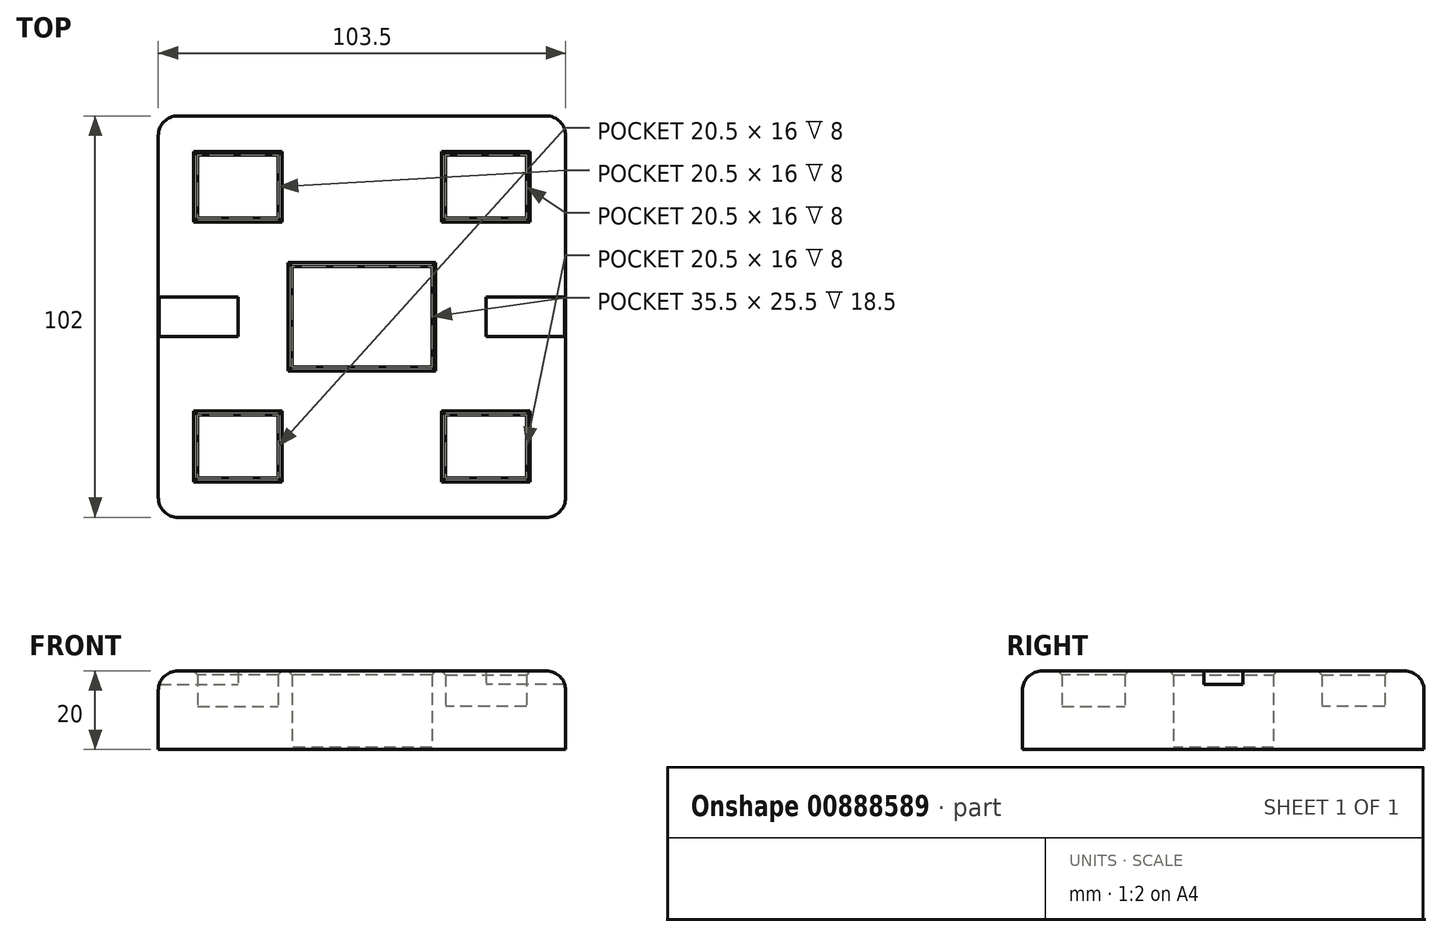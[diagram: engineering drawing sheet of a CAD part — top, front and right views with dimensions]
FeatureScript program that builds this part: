
annotation { "Feature Type Name" : "Feature", "Feature Type Description" : "" }
export const myFeature = defineFeature(function(context is Context, id is Id, definition is map)
    precondition{}
    {
        {
            var Q0;
            Q0=qCreatedBy(makeId("Top.planeOp"),FACE);
            var sketch = newSketch(context, id + "F0", { "sketchPlane" : qUnion([Q0])});
            skLineSegment(sketch, "E0.bottom", {"start": v(-46.75, 51) * mm, "end": v(46.75, 51) * mm});
            skLineSegment(sketch, "E0.top", {"start": v(-46.75, -51) * mm, "end": v(46.75, -51) * mm});
            skLineSegment(sketch, "E0.left", {"start": v(-51.75, 46) * mm, "end": v(-51.75, -46) * mm});
            skLineSegment(sketch, "E0.right", {"start": v(51.75, 46) * mm, "end": v(51.75, -46) * mm});
            skPoint(sketch, "E0.middle", {"position": v(0, 0) * mm});
            skLineSegment(sketch, "E1", {"start": v(-41.75, 51) * mm, "end": v(-41.75, -51) * mm});
            skLineSegment(sketch, "E2", {"start": v(-51.75, 41) * mm, "end": v(51.75, 41) * mm});
            skLineSegment(sketch, "E3", {"start": v(41.75, 51) * mm, "end": v(41.75, -51) * mm});
            skLineSegment(sketch, "E4", {"start": v(-51.75, -41) * mm, "end": v(51.75, -41) * mm});
            skLineSegment(sketch, "E5.bottom", {"start": v(-41.75, 41) * mm, "end": v(-21.25, 41) * mm});
            skLineSegment(sketch, "E5.top", {"start": v(-41.75, 25) * mm, "end": v(-21.25, 25) * mm});
            skLineSegment(sketch, "E5.left", {"start": v(-41.75, 41) * mm, "end": v(-41.75, 25) * mm});
            skLineSegment(sketch, "E5.right", {"start": v(-21.25, 41) * mm, "end": v(-21.25, 25) * mm});
            skLineSegment(sketch, "E6.bottom", {"start": v(41.75, 41) * mm, "end": v(21.25, 41) * mm});
            skLineSegment(sketch, "E6.top", {"start": v(41.75, 25) * mm, "end": v(21.25, 25) * mm});
            skLineSegment(sketch, "E6.left", {"start": v(41.75, 41) * mm, "end": v(41.75, 25) * mm});
            skLineSegment(sketch, "E6.right", {"start": v(21.25, 41) * mm, "end": v(21.25, 25) * mm});
            skLineSegment(sketch, "E7.bottom", {"start": v(-41.75, -41) * mm, "end": v(-21.25, -41) * mm});
            skLineSegment(sketch, "E7.top", {"start": v(-41.75, -25) * mm, "end": v(-21.25, -25) * mm});
            skLineSegment(sketch, "E7.left", {"start": v(-41.75, -41) * mm, "end": v(-41.75, -25) * mm});
            skLineSegment(sketch, "E7.right", {"start": v(-21.25, -41) * mm, "end": v(-21.25, -25) * mm});
            skLineSegment(sketch, "E8.bottom", {"start": v(41.75, -41) * mm, "end": v(21.25, -41) * mm});
            skLineSegment(sketch, "E8.top", {"start": v(41.75, -25) * mm, "end": v(21.25, -25) * mm});
            skLineSegment(sketch, "E8.left", {"start": v(41.75, -41) * mm, "end": v(41.75, -25) * mm});
            skLineSegment(sketch, "E8.right", {"start": v(21.25, -41) * mm, "end": v(21.25, -25) * mm});
            skLineSegment(sketch, "E9.bottom", {"start": v(17.75, 12.75) * mm, "end": v(-17.75, 12.75) * mm});
            skLineSegment(sketch, "E9.top", {"start": v(17.75, -12.75) * mm, "end": v(-17.75, -12.75) * mm});
            skLineSegment(sketch, "E9.left", {"start": v(17.75, 12.75) * mm, "end": v(17.75, -12.75) * mm});
            skLineSegment(sketch, "E9.right", {"start": v(-17.75, 12.75) * mm, "end": v(-17.75, -12.75) * mm});
            skPoint(sketch, "E10.visualSharp", {"position": v(-51.75, 51) * mm});
            skArc(sketch, "E10.filletArc", {"start": v(-46.75, 51) * mm, "mid": v(-50.29, 49.54) * mm, "end": v(-51.75, 46) * mm});
            skPoint(sketch, "E11.visualSharp", {"position": v(51.75, 51) * mm});
            skArc(sketch, "E11.filletArc", {"start": v(51.75, 46) * mm, "mid": v(50.29, 49.54) * mm, "end": v(46.75, 51) * mm});
            skPoint(sketch, "E12.visualSharp", {"position": v(51.75, -51) * mm});
            skArc(sketch, "E12.filletArc", {"start": v(46.75, -51) * mm, "mid": v(50.29, -49.54) * mm, "end": v(51.75, -46) * mm});
            skPoint(sketch, "E13.visualSharp", {"position": v(-51.75, -51) * mm});
            skArc(sketch, "E13.filletArc", {"start": v(-51.75, -46) * mm, "mid": v(-50.29, -49.54) * mm, "end": v(-46.75, -51) * mm});
            skLineSegment(sketch, "E14.bottom", {"start": v(-51.75, -5) * mm, "end": v(-31.5, -5) * mm});
            skLineSegment(sketch, "E14.top", {"start": v(-51.75, 5) * mm, "end": v(-31.5, 5) * mm});
            skLineSegment(sketch, "E14.left", {"start": v(-51.75, -5) * mm, "end": v(-51.75, 5) * mm});
            skLineSegment(sketch, "E14.right", {"start": v(-31.5, -5) * mm, "end": v(-31.5, 5) * mm});
            skLineSegment(sketch, "E15.bottom", {"start": v(51.75, -5) * mm, "end": v(31.5, -5) * mm});
            skLineSegment(sketch, "E15.top", {"start": v(51.75, 5) * mm, "end": v(31.5, 5) * mm});
            skLineSegment(sketch, "E15.left", {"start": v(51.75, -5) * mm, "end": v(51.75, 5) * mm});
            skLineSegment(sketch, "E15.right", {"start": v(31.5, -5) * mm, "end": v(31.5, 5) * mm});
            skSolve(sketch);
        }
        {
            assignVariable(context, id + "F1", {"name" : "DickeP", "anyValue" : 20 * mm});
        }
        {
            var Q0;
            {var subQ0=sQuery(id+"F0.wireOp",EDGE,"E10.filletArc");Q0=makeQuery(id+"F0.imprint","IMPRINT",FACE,{"disambiguationData":[TD([[makeQuery(id+"F0.imprint","IMPRINT",EDGE,{"derivedFrom":subQ0}),1.0]])]});}
            var Q1;
            {var subQ4=sQuery(id+"F0.wireOp",EDGE,"E0.left");var subQ6=sQuery(id+"F0.wireOp",EDGE,"E14.top");var subQ8=makeQuery(id+"F0.imprint","INTERSECT",VERTEX,{"derivedFrom":[subQ4,subQ6]});Q1=makeQuery(id+"F0.imprint","IMPRINT",FACE,{"disambiguationData":[TD([[makeQuery(id+"F0.imprint","IMPRINT",EDGE,{"disambiguationData":[TD([[subQ8,1.0]])],"derivedFrom":subQ4}),1.0]])]});}
            var Q2;
            {var subQ1=sQuery(id+"F0.wireOp",EDGE,"E0.left");var subQ5=sQuery(id+"F0.wireOp",EDGE,"E14.bottom");var subQ8=makeQuery(id+"F0.imprint","INTERSECT",VERTEX,{"derivedFrom":[subQ1,subQ5]});Q2=makeQuery(id+"F0.imprint","IMPRINT",FACE,{"disambiguationData":[TD([[makeQuery(id+"F0.imprint","IMPRINT",EDGE,{"disambiguationData":[TD([[subQ8,-1.0]])],"derivedFrom":subQ1}),1.0]])]});}
            var Q3;
            {var subQ7=sQuery(id+"F0.wireOp",EDGE,"E13.filletArc");Q3=makeQuery(id+"F0.imprint","IMPRINT",FACE,{"disambiguationData":[TD([[makeQuery(id+"F0.imprint","IMPRINT",EDGE,{"derivedFrom":subQ7}),1.0]])]});}
            var Q4;
            {var subQ4=sQuery(id+"F0.wireOp",EDGE,"E0.top");var subQ7=sQuery(id+"F0.wireOp",EDGE,"E1");var subQ8=makeQuery(id+"F0.imprint","INTERSECT",VERTEX,{"derivedFrom":[subQ4,subQ7]});Q4=makeQuery(id+"F0.imprint","IMPRINT",FACE,{"disambiguationData":[TD([[makeQuery(id+"F0.imprint","IMPRINT",EDGE,{"disambiguationData":[TD([[subQ8,-1.0]])],"derivedFrom":subQ4}),1.0]])]});}
            var Q5;
            {var subQ0=sQuery(id+"F0.wireOp",EDGE,"E12.filletArc");Q5=makeQuery(id+"F0.imprint","IMPRINT",FACE,{"disambiguationData":[TD([[makeQuery(id+"F0.imprint","IMPRINT",EDGE,{"derivedFrom":subQ0}),1.0]])]});}
            var Q6;
            {var subQ2=sQuery(id+"F0.wireOp",EDGE,"E4");var subQ4=sQuery(id+"F0.wireOp",EDGE,"E0.right");var subQ5=makeQuery(id+"F0.imprint","INTERSECT",VERTEX,{"derivedFrom":[subQ4,subQ2]});Q6=makeQuery(id+"F0.imprint","IMPRINT",FACE,{"disambiguationData":[TD([[makeQuery(id+"F0.imprint","IMPRINT",EDGE,{"disambiguationData":[TD([[subQ5,1.0]])],"derivedFrom":subQ4}),-1.0]])]});}
            var Q7;
            {var subQ18=sQuery(id+"F0.wireOp",EDGE,"E5.top");Q7=makeQuery(id+"F0.imprint","IMPRINT",FACE,{"disambiguationData":[TD([[makeQuery(id+"F0.imprint","IMPRINT",EDGE,{"derivedFrom":subQ18}),-1.0]])]});}
            var Q8;
            {var subQ4=sQuery(id+"F0.wireOp",EDGE,"E2");var subQ6=sQuery(id+"F0.wireOp",EDGE,"E0.right");var subQ8=makeQuery(id+"F0.imprint","INTERSECT",VERTEX,{"derivedFrom":[subQ6,subQ4]});Q8=makeQuery(id+"F0.imprint","IMPRINT",FACE,{"disambiguationData":[TD([[makeQuery(id+"F0.imprint","IMPRINT",EDGE,{"disambiguationData":[TD([[subQ8,-1.0]])],"derivedFrom":subQ6}),-1.0]])]});}
            var Q9;
            {var subQ5=sQuery(id+"F0.wireOp",EDGE,"E1");var subQ6=sQuery(id+"F0.wireOp",EDGE,"E0.bottom");var subQ7=makeQuery(id+"F0.imprint","INTERSECT",VERTEX,{"derivedFrom":[subQ6,subQ5]});Q9=makeQuery(id+"F0.imprint","IMPRINT",FACE,{"disambiguationData":[TD([[makeQuery(id+"F0.imprint","IMPRINT",EDGE,{"disambiguationData":[TD([[subQ7,-1.0]])],"derivedFrom":subQ6}),-1.0]])]});}
            var Q10;
            {var subQ7=sQuery(id+"F0.wireOp",EDGE,"E11.filletArc");Q10=makeQuery(id+"F0.imprint","IMPRINT",FACE,{"disambiguationData":[TD([[makeQuery(id+"F0.imprint","IMPRINT",EDGE,{"derivedFrom":subQ7}),1.0]])]});}
            extrude(context, id + "F2", {"entities" : qUnion([Q0, Q1, Q2, Q3, Q4, Q5, Q6, Q7, Q8, Q9, Q10]), "depth" : getVariable(context, 'DickeP'), "offsetDistance" : 25 * mm});
        }
        {
            assignVariable(context, id + "F3", {"name" : "unterLochST", "anyValue" : 11 * mm});
        }
        {
            var Q0;
            {var subQ3=sQuery(id+"F0.wireOp",EDGE,"E5.top");Q0=makeQuery(id+"F0.imprint","IMPRINT",FACE,{"disambiguationData":[TD([[makeQuery(id+"F0.imprint","IMPRINT",EDGE,{"derivedFrom":subQ3}),1.0]])]});}
            var Q1;
            {var subQ4=sQuery(id+"F0.wireOp",EDGE,"E6.top");Q1=makeQuery(id+"F0.imprint","IMPRINT",FACE,{"disambiguationData":[TD([[makeQuery(id+"F0.imprint","IMPRINT",EDGE,{"derivedFrom":subQ4}),-1.0]])]});}
            var Q2;
            {var subQ0=sQuery(id+"F0.wireOp",EDGE,"E8.top");Q2=makeQuery(id+"F0.imprint","IMPRINT",FACE,{"disambiguationData":[TD([[makeQuery(id+"F0.imprint","IMPRINT",EDGE,{"derivedFrom":subQ0}),1.0]])]});}
            var Q3;
            {var subQ0=sQuery(id+"F0.wireOp",EDGE,"E7.top");Q3=makeQuery(id+"F0.imprint","IMPRINT",FACE,{"disambiguationData":[TD([[makeQuery(id+"F0.imprint","IMPRINT",EDGE,{"derivedFrom":subQ0}),-1.0]])]});}
            extrude(context, id + "F4", {"entities" : qUnion([Q0, Q1, Q2, Q3]), "operationType" : NewBodyOperationType.ADD, "depth" : getVariable(context, 'unterLochST'), "offsetDistance" : 25 * mm});
        }
        {
            assignVariable(context, id + "F5", {"name" : "unterLochRM", "anyValue" : 0.5});
        }
        {
            var Q0;
            Q0=makeQuery(id+"F0.imprint","IMPRINT",FACE,{"disambiguationData":[TD([[makeQuery(id+"F0.imprint","IMPRINT",EDGE,{"derivedFrom":sQuery(id+"F0.wireOp",EDGE,"E9.bottom")}),1.0]])]});
            extrude(context, id + "F6", {"entities" : qUnion([Q0]), "operationType" : NewBodyOperationType.ADD, "depth" : (getVariable(context, 'unterLochRM')) * mm, "offsetDistance" : 25 * mm});
        }
        {
            var Q0;
            {var subQ5=sQuery(id+"F0.wireOp",EDGE,"E14.right");Q0=makeQuery(id+"F0.imprint","IMPRINT",FACE,{"disambiguationData":[TD([[makeQuery(id+"F0.imprint","IMPRINT",EDGE,{"derivedFrom":subQ5}),1.0]])]});}
            var Q1;
            {var subQ0=sQuery(id+"F0.wireOp",EDGE,"E14.bottom");var subQ1=sQuery(id+"F0.wireOp",EDGE,"E0.left");var subQ2=makeQuery(id+"F0.imprint","INTERSECT",VERTEX,{"derivedFrom":[subQ1,subQ0]});Q1=makeQuery(id+"F0.imprint","IMPRINT",FACE,{"disambiguationData":[TD([[makeQuery(id+"F0.imprint","IMPRINT",EDGE,{"disambiguationData":[TD([[subQ2,1.0]])],"derivedFrom":subQ1}),1.0]])]});}
            var Q2;
            {var subQ5=sQuery(id+"F0.wireOp",EDGE,"E15.right");Q2=makeQuery(id+"F0.imprint","IMPRINT",FACE,{"disambiguationData":[TD([[makeQuery(id+"F0.imprint","IMPRINT",EDGE,{"derivedFrom":subQ5}),-1.0]])]});}
            var Q3;
            {var subQ0=sQuery(id+"F0.wireOp",EDGE,"E15.top");var subQ1=sQuery(id+"F0.wireOp",EDGE,"E0.right");var subQ2=makeQuery(id+"F0.imprint","INTERSECT",VERTEX,{"derivedFrom":[subQ1,subQ0]});Q3=makeQuery(id+"F0.imprint","IMPRINT",FACE,{"disambiguationData":[TD([[makeQuery(id+"F0.imprint","IMPRINT",EDGE,{"disambiguationData":[TD([[subQ2,-1.0]])],"derivedFrom":subQ1}),-1.0]])]});}
            extrude(context, id + "F7", {"entities" : qUnion([Q0, Q1, Q2, Q3]), "operationType" : NewBodyOperationType.ADD, "depth" : 16.5 * mm, "offsetDistance" : 25 * mm});
        }
        {
            var Q0;
            {var subQ0=sQuery(id+"F0.wireOp",EDGE,"E2");Q0=makeQuery(id+"F2.opExtrude","CAP_EDGE",EDGE,{"disambiguationData":[OSD([subQ0]),TDD([makeQuery(id+"F0.imprint","IMPRINT",EDGE,{"disambiguationData":[TD([[makeQuery(id+"F0.imprint","INTERSECT",VERTEX,{"derivedFrom":[sQuery(id+"F0.wireOp",EDGE,"E1"),subQ0]}),-1.0]])],"derivedFrom":subQ0})])],"isStart":false});}
            var Q1;
            Q1=makeQuery(id+"F2.opExtrude","CAP_EDGE",EDGE,{"disambiguationData":[OSD([sQuery(id+"F0.wireOp",EDGE,"E5.right")])],"isStart":false});
            var Q2;
            {var subQ0=sQuery(id+"F0.wireOp",EDGE,"E1");Q2=makeQuery(id+"F2.opExtrude","CAP_EDGE",EDGE,{"disambiguationData":[OSD([subQ0]),TDD([makeQuery(id+"F0.imprint","IMPRINT",EDGE,{"disambiguationData":[TD([[makeQuery(id+"F0.imprint","INTERSECT",VERTEX,{"derivedFrom":[subQ0,sQuery(id+"F0.wireOp",EDGE,"E2")]}),-1.0]])],"derivedFrom":subQ0})])],"isStart":false});}
            var Q3;
            Q3=makeQuery(id+"F2.opExtrude","CAP_EDGE",EDGE,{"disambiguationData":[OSD([sQuery(id+"F0.wireOp",EDGE,"E5.top")])],"isStart":false});
            var Q4;
            {var subQ0=sQuery(id+"F0.wireOp",EDGE,"E2");Q4=makeQuery(id+"F2.opExtrude","CAP_EDGE",EDGE,{"disambiguationData":[OSD([subQ0]),TDD([makeQuery(id+"F0.imprint","IMPRINT",EDGE,{"disambiguationData":[TD([[makeQuery(id+"F0.imprint","INTERSECT",VERTEX,{"derivedFrom":[subQ0,sQuery(id+"F0.wireOp",EDGE,"E6.right")]}),-1.0]])],"derivedFrom":subQ0})])],"isStart":false});}
            var Q5;
            Q5=makeQuery(id+"F2.opExtrude","CAP_EDGE",EDGE,{"disambiguationData":[OSD([sQuery(id+"F0.wireOp",EDGE,"E6.right")])],"isStart":false});
            var Q6;
            Q6=makeQuery(id+"F2.opExtrude","CAP_EDGE",EDGE,{"disambiguationData":[OSD([sQuery(id+"F0.wireOp",EDGE,"E6.top")])],"isStart":false});
            var Q7;
            {var subQ0=sQuery(id+"F0.wireOp",EDGE,"E3");Q7=makeQuery(id+"F2.opExtrude","CAP_EDGE",EDGE,{"disambiguationData":[OSD([subQ0]),TDD([makeQuery(id+"F0.imprint","IMPRINT",EDGE,{"disambiguationData":[TD([[makeQuery(id+"F0.imprint","INTERSECT",VERTEX,{"derivedFrom":[subQ0,sQuery(id+"F0.wireOp",EDGE,"E6.top")]}),1.0]])],"derivedFrom":subQ0})])],"isStart":false});}
            var Q8;
            Q8=makeQuery(id+"F2.opExtrude","CAP_EDGE",EDGE,{"disambiguationData":[OSD([sQuery(id+"F0.wireOp",EDGE,"E8.top")])],"isStart":false});
            var Q9;
            Q9=makeQuery(id+"F2.opExtrude","CAP_EDGE",EDGE,{"disambiguationData":[OSD([sQuery(id+"F0.wireOp",EDGE,"E8.right")])],"isStart":false});
            var Q10;
            {var subQ0=sQuery(id+"F0.wireOp",EDGE,"E4");Q10=makeQuery(id+"F2.opExtrude","CAP_EDGE",EDGE,{"disambiguationData":[OSD([subQ0]),TDD([makeQuery(id+"F0.imprint","IMPRINT",EDGE,{"disambiguationData":[TD([[makeQuery(id+"F0.imprint","INTERSECT",VERTEX,{"derivedFrom":[subQ0,sQuery(id+"F0.wireOp",EDGE,"E8.right")]}),-1.0]])],"derivedFrom":subQ0})])],"isStart":false});}
            var Q11;
            {var subQ0=sQuery(id+"F0.wireOp",EDGE,"E3");Q11=makeQuery(id+"F2.opExtrude","CAP_EDGE",EDGE,{"disambiguationData":[OSD([subQ0]),TDD([makeQuery(id+"F0.imprint","IMPRINT",EDGE,{"disambiguationData":[TD([[makeQuery(id+"F0.imprint","INTERSECT",VERTEX,{"derivedFrom":[subQ0,sQuery(id+"F0.wireOp",EDGE,"E8.top")]}),-1.0]])],"derivedFrom":subQ0})])],"isStart":false});}
            var Q12;
            Q12=makeQuery(id+"F2.opExtrude","CAP_EDGE",EDGE,{"disambiguationData":[OSD([sQuery(id+"F0.wireOp",EDGE,"E7.top")])],"isStart":false});
            var Q13;
            {var subQ0=sQuery(id+"F0.wireOp",EDGE,"E1");Q13=makeQuery(id+"F2.opExtrude","CAP_EDGE",EDGE,{"disambiguationData":[OSD([subQ0]),TDD([makeQuery(id+"F0.imprint","IMPRINT",EDGE,{"disambiguationData":[TD([[makeQuery(id+"F0.imprint","INTERSECT",VERTEX,{"derivedFrom":[subQ0,sQuery(id+"F0.wireOp",EDGE,"E7.top")]}),-1.0]])],"derivedFrom":subQ0})])],"isStart":false});}
            var Q14;
            {var subQ0=sQuery(id+"F0.wireOp",EDGE,"E4");Q14=makeQuery(id+"F2.opExtrude","CAP_EDGE",EDGE,{"disambiguationData":[OSD([subQ0]),TDD([makeQuery(id+"F0.imprint","IMPRINT",EDGE,{"disambiguationData":[TD([[makeQuery(id+"F0.imprint","INTERSECT",VERTEX,{"derivedFrom":[subQ0,sQuery(id+"F0.wireOp",EDGE,"E7.right")]}),1.0]])],"derivedFrom":subQ0})])],"isStart":false});}
            var Q15;
            Q15=makeQuery(id+"F2.opExtrude","CAP_EDGE",EDGE,{"disambiguationData":[OSD([sQuery(id+"F0.wireOp",EDGE,"E7.right")])],"isStart":false});
            chamfer(context, id + "F8", {"entities" : qUnion([Q0, Q1, Q2, Q3, Q4, Q5, Q6, Q7, Q8, Q9, Q10, Q11, Q12, Q13, Q14, Q15]), "width" : 1 * mm, "tangentPropagation" : true});
        }
        {
            var Q0;
            {var subQ0=sQuery(id+"F0.wireOp",EDGE,"E0.left");Q0=makeQuery(id+"F2.opExtrude","CAP_EDGE",EDGE,{"disambiguationData":[OSD([subQ0]),TDD([makeQuery(id+"F0.imprint","IMPRINT",EDGE,{"disambiguationData":[TD([[makeQuery(id+"F0.imprint","INTERSECT",VERTEX,{"derivedFrom":[subQ0,sQuery(id+"F0.wireOp",EDGE,"E14.bottom")]}),-1.0]])],"derivedFrom":subQ0}),makeQuery(id+"F0.imprint","IMPRINT",EDGE,{"disambiguationData":[TD([[makeQuery(id+"F0.imprint","INTERSECT",VERTEX,{"derivedFrom":[subQ0,sQuery(id+"F0.wireOp",EDGE,"E13.filletArc")]}),1.0]])],"derivedFrom":subQ0})])],"isStart":false});}
            var Q1;
            {var subQ0=sQuery(id+"F0.wireOp",EDGE,"E0.right");var subQ1=makeQuery(id+"F0.imprint","INTERSECT",VERTEX,{"derivedFrom":[subQ0,sQuery(id+"F0.wireOp",EDGE,"E2")]});Q1=makeQuery(id+"F2.opExtrude","CAP_EDGE",EDGE,{"disambiguationData":[OSD([subQ0]),TDD([makeQuery(id+"F0.imprint","IMPRINT",EDGE,{"disambiguationData":[TD([[subQ1,-1.0]])],"derivedFrom":subQ0}),makeQuery(id+"F0.imprint","IMPRINT",EDGE,{"disambiguationData":[TD([[subQ1,1.0]])],"derivedFrom":subQ0})])],"isStart":false});}
            fillet(context, id + "F9", {"entities" : qUnion([Q0, Q1]), "radius" : 5 * mm, "tangentPropagation" : true, "allowEdgeOverflow" : false});
        }
        {
            var Q0;
            Q0=makeQuery(id+"F2.opExtrude","CAP_EDGE",EDGE,{"disambiguationData":[OSD([sQuery(id+"F0.wireOp",EDGE,"E9.top")])],"isStart":false});
            var Q1;
            Q1=makeQuery(id+"F2.opExtrude","CAP_EDGE",EDGE,{"disambiguationData":[OSD([sQuery(id+"F0.wireOp",EDGE,"E9.right")])],"isStart":false});
            var Q2;
            Q2=makeQuery(id+"F2.opExtrude","CAP_EDGE",EDGE,{"disambiguationData":[OSD([sQuery(id+"F0.wireOp",EDGE,"E9.bottom")])],"isStart":false});
            var Q3;
            Q3=makeQuery(id+"F2.opExtrude","CAP_EDGE",EDGE,{"disambiguationData":[OSD([sQuery(id+"F0.wireOp",EDGE,"E9.left")])],"isStart":false});
            chamfer(context, id + "F10", {"entities" : qUnion([Q0, Q1, Q2, Q3]), "width" : 1 * mm, "tangentPropagation" : true});
        }
    });
